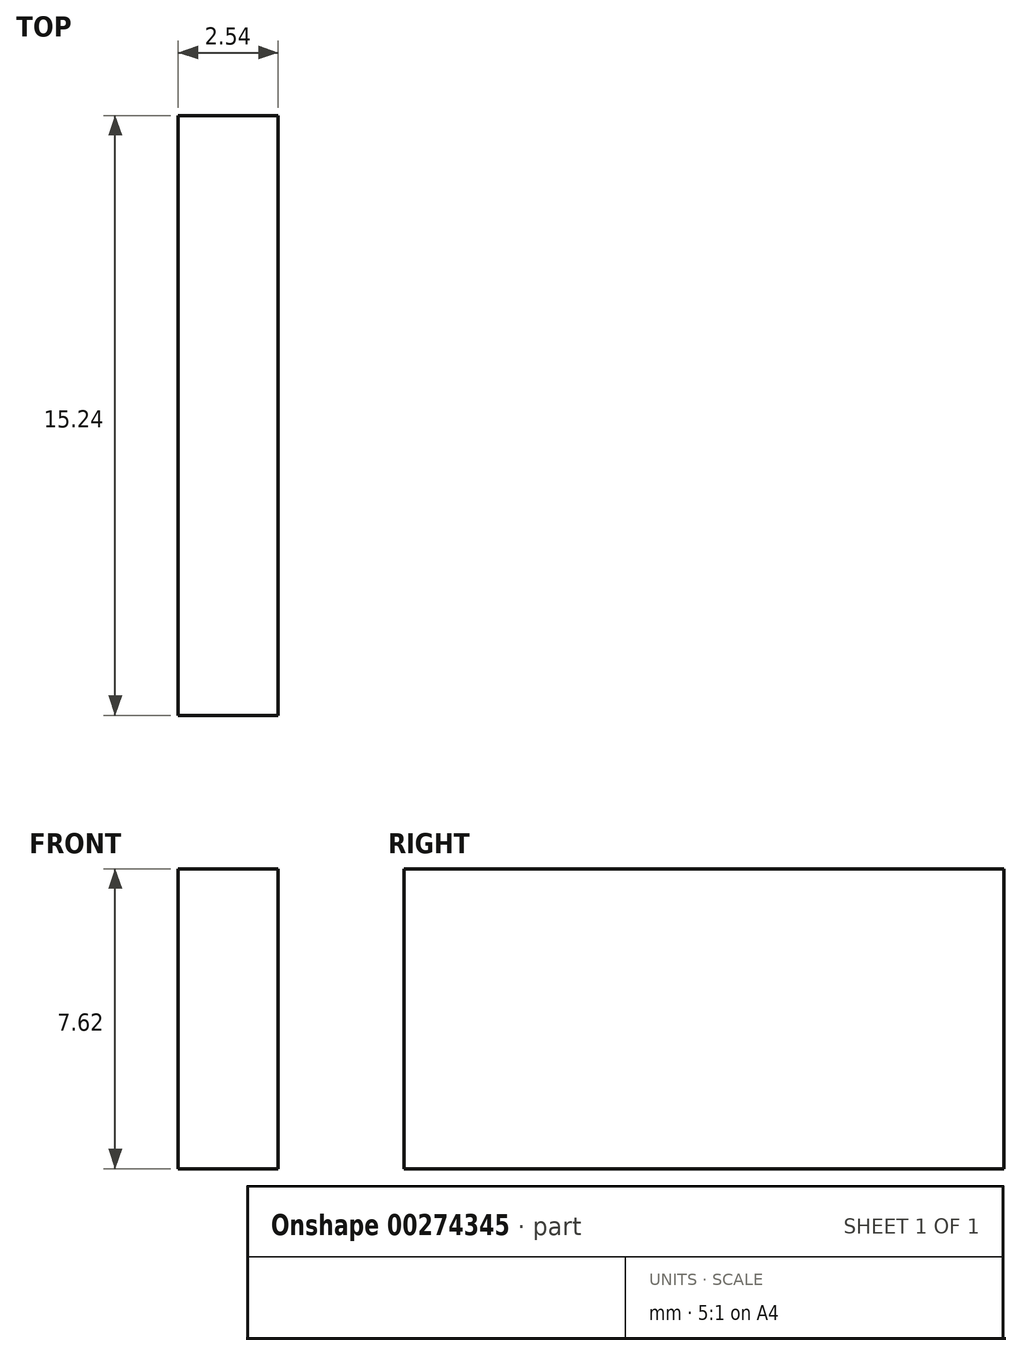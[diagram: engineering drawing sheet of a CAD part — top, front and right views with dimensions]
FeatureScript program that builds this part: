
annotation { "Feature Type Name" : "Feature", "Feature Type Description" : "" }
export const myFeature = defineFeature(function(context is Context, id is Id, definition is map)
    precondition{}
    {
        {
            var Q0;
            Q0=qCreatedBy(makeId("Front.planeOp"),FACE);
            var sketch = newSketch(context, id + "F0", { "sketchPlane" : qUnion([Q0])});
            skLineSegment(sketch, "E0.bottom", {"start": v(-2.54, 16.9) * mm, "end": v(0, 16.9) * mm});
            skLineSegment(sketch, "E0.top", {"start": v(-2.54, 9.29) * mm, "end": v(0, 9.29) * mm});
            skLineSegment(sketch, "E0.left", {"start": v(-2.54, 16.9) * mm, "end": v(-2.54, 9.29) * mm});
            skLineSegment(sketch, "E0.right", {"start": v(0, 16.9) * mm, "end": v(0, 9.29) * mm});
            skSolve(sketch);
        }
        {
            var Q0;
            Q0=makeQuery(id+"F0.imprint","IMPRINT",FACE,{"disambiguationData":[TD([[makeQuery(id+"F0.imprint","IMPRINT",EDGE,{"derivedFrom":sQuery(id+"F0.wireOp",EDGE,"E0.bottom")}),-1.0]])]});
            extrude(context, id + "F1", {"entities" : qUnion([Q0]), "depth" : 15.24 * mm});
        }
    });
